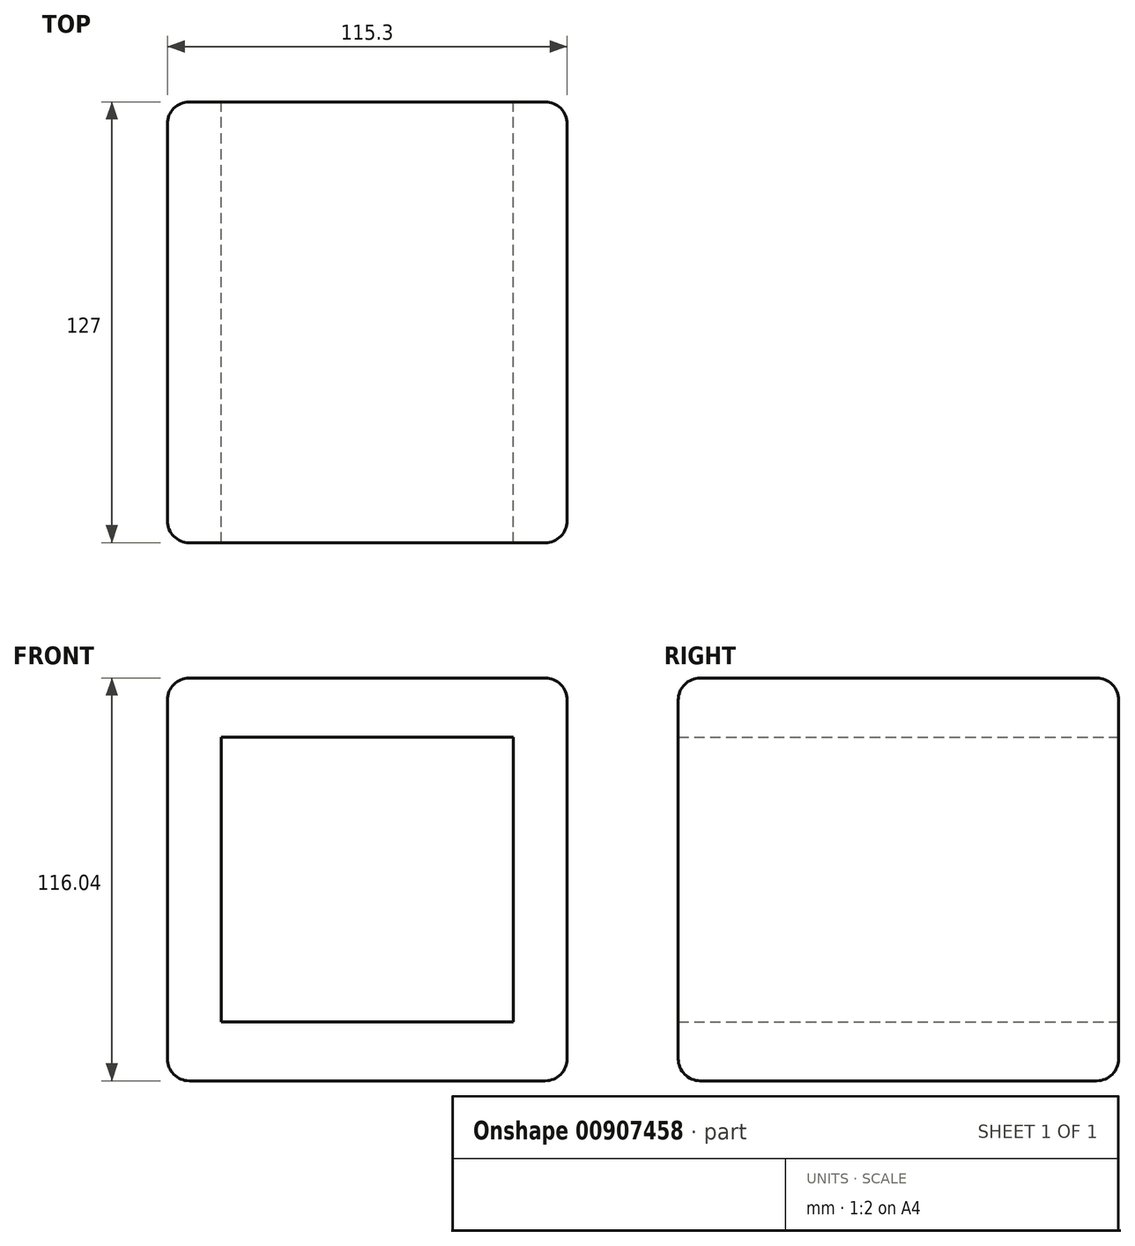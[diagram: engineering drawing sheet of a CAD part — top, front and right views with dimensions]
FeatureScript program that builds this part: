
annotation { "Feature Type Name" : "Feature", "Feature Type Description" : "" }
export const myFeature = defineFeature(function(context is Context, id is Id, definition is map)
    precondition{}
    {
        {
            var Q0;
            Q0=qCreatedBy(makeId("Front.planeOp"),FACE);
            var sketch = newSketch(context, id + "F0", { "sketchPlane" : qUnion([Q0])});
            skLineSegment(sketch, "E0.bottom", {"start": v(-42.13, -41.02) * mm, "end": v(42.13, -41.02) * mm});
            skLineSegment(sketch, "E0.top", {"start": v(-42.13, 41.02) * mm, "end": v(42.13, 41.02) * mm});
            skLineSegment(sketch, "E0.left", {"start": v(-42.13, -41.02) * mm, "end": v(-42.13, 41.02) * mm});
            skLineSegment(sketch, "E0.right", {"start": v(42.13, -41.02) * mm, "end": v(42.13, 41.02) * mm});
            skPoint(sketch, "E0.middle", {"position": v(0, 0) * mm});
            skLineSegment(sketch, "E1.bottom", {"start": v(-57.65, -58.02) * mm, "end": v(57.65, -58.02) * mm});
            skLineSegment(sketch, "E1.top", {"start": v(-57.65, 58.02) * mm, "end": v(57.65, 58.02) * mm});
            skLineSegment(sketch, "E1.left", {"start": v(-57.65, -58.02) * mm, "end": v(-57.65, 58.02) * mm});
            skLineSegment(sketch, "E1.right", {"start": v(57.65, -58.02) * mm, "end": v(57.65, 58.02) * mm});
            skSolve(sketch);
        }
        {
            var Q0;
            Q0=makeQuery(id+"F0.imprint","IMPRINT",FACE,{"disambiguationData":[TD([[makeQuery(id+"F0.imprint","IMPRINT",EDGE,{"derivedFrom":sQuery(id+"F0.wireOp",EDGE,"E0.bottom")}),-1.0]])]});
            extrude(context, id + "F1", {"entities" : qUnion([Q0]), "depth" : 127 * mm, "offsetDistance" : 25.4 * mm});
        }
        {
            var Q0;
            Q0=makeQuery(id+"F1.opExtrude","SWEPT_EDGE",EDGE,{"disambiguationData":[OSD([sQuery(id+"F0.wireOp",EDGE,"E1.top"),sQuery(id+"F0.wireOp",EDGE,"E1.left")])]});
            var Q1;
            Q1=makeQuery(id+"F1.opExtrude","SWEPT_FACE",FACE,{"disambiguationData":[OSD([sQuery(id+"F0.wireOp",EDGE,"E1.left")])]});
            var Q2;
            Q2=makeQuery(id+"F1.opExtrude","SWEPT_FACE",FACE,{"disambiguationData":[OSD([sQuery(id+"F0.wireOp",EDGE,"E1.bottom")])]});
            var Q3;
            Q3=makeQuery(id+"F1.opExtrude","SWEPT_FACE",FACE,{"disambiguationData":[OSD([sQuery(id+"F0.wireOp",EDGE,"E1.right")])]});
            var Q4;
            Q4=makeQuery(id+"F1.opExtrude","SWEPT_FACE",FACE,{"disambiguationData":[OSD([sQuery(id+"F0.wireOp",EDGE,"E1.top")])]});
            fillet(context, id + "F2", {"entities" : qUnion([Q0, Q1, Q2, Q3, Q4]), "radius" : 6.35 * mm, "tangentPropagation" : true, "allowEdgeOverflow" : false});
        }
    });
